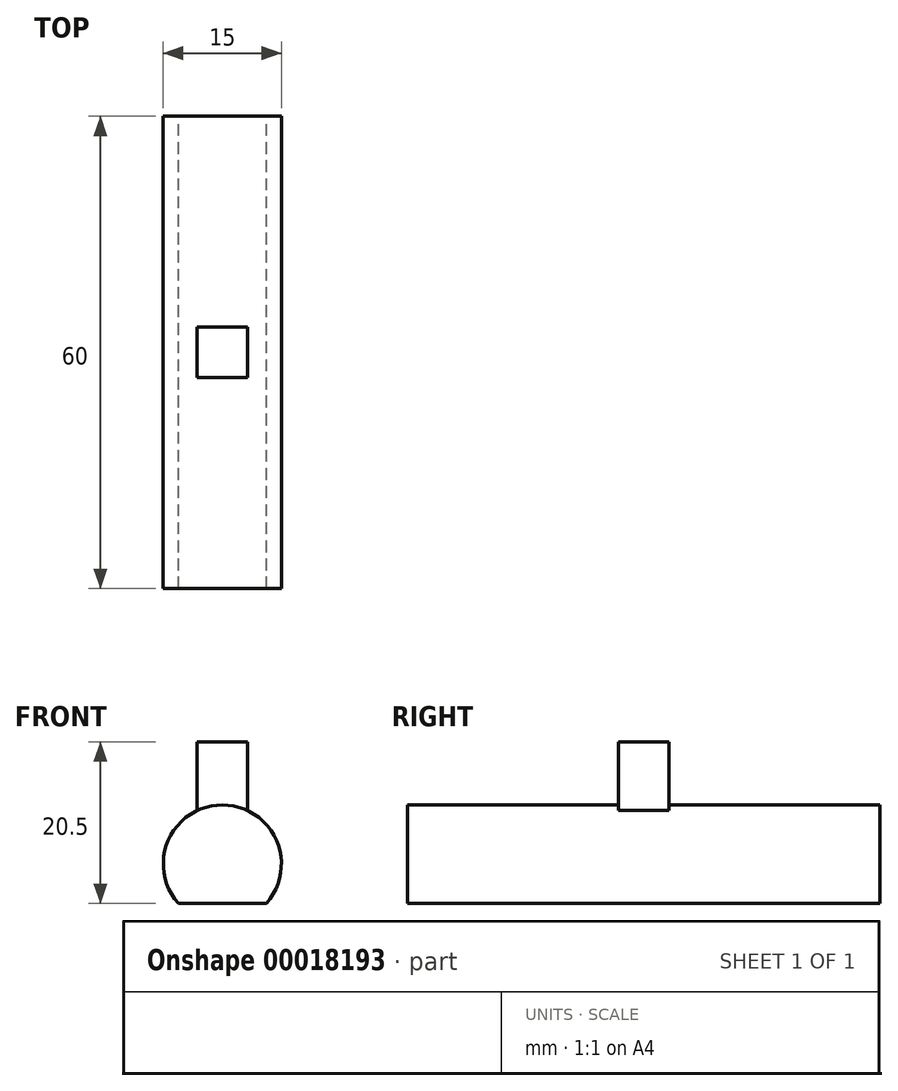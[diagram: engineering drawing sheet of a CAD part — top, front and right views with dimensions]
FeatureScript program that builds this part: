
annotation { "Feature Type Name" : "Feature", "Feature Type Description" : "" }
export const myFeature = defineFeature(function(context is Context, id is Id, definition is map)
    precondition{}
    {
        {
            var Q0;
            Q0=qCreatedBy(makeId("Front.planeOp"),FACE);
            var sketch = newSketch(context, id + "F0", { "sketchPlane" : qUnion([Q0])});
            skArc(sketch, "E0", {"start": v(5.6, 0) * mm, "mid": v(0, 12.5) * mm, "end": v(-5.6, 0) * mm});
            skLineSegment(sketch, "E1", {"start": v(-5.6, 0) * mm, "end": v(5.6, 0) * mm});
            skSolve(sketch);
        }
        {
            var Q0;
            Q0=makeQuery(id+"F0.imprint","IMPRINT",FACE,{"disambiguationData":[TD([[makeQuery(id+"F0.imprint","IMPRINT",EDGE,{"derivedFrom":sQuery(id+"F0.wireOp",EDGE,"E0")}),1.0]])]});
            extrude(context, id + "F1", {"entities" : qUnion([Q0]), "endBound" : BoundingType.SYMMETRIC, "depth" : 60 * mm});
        }
        {
            var Q0;
            Q0=makeQuery(id+"F1.opExtrude","SWEPT_FACE",FACE,{"disambiguationData":[OSD([sQuery(id+"F0.wireOp",EDGE,"E1")])]});
            var sketch = newSketch(context, id + "F2", { "sketchPlane" : qUnion([Q0])});
            skLineSegment(sketch, "E2.bottom", {"start": v(-3.2, 3.2) * mm, "end": v(3.2, 3.2) * mm});
            skLineSegment(sketch, "E2.top", {"start": v(-3.2, -3.2) * mm, "end": v(3.2, -3.2) * mm});
            skLineSegment(sketch, "E2.left", {"start": v(-3.2, 3.2) * mm, "end": v(-3.2, -3.2) * mm});
            skLineSegment(sketch, "E2.right", {"start": v(3.2, 3.2) * mm, "end": v(3.2, -3.2) * mm});
            skPoint(sketch, "E2.middle", {"position": v(0, 0) * mm});
            skSolve(sketch);
        }
        {
            var Q0;
            Q0=makeQuery(id+"F2.imprint","IMPRINT",FACE,{"disambiguationData":[TD([[makeQuery(id+"F2.imprint","IMPRINT",EDGE,{"derivedFrom":sQuery(id+"F2.wireOp",EDGE,"E2.bottom")}),-1.0]])]});
            extrude(context, id + "F3", {"entities" : qUnion([Q0]), "operationType" : NewBodyOperationType.ADD, "oppositeDirection" : true, "depth" : (12.5 + 8) * mm});
        }
    });
